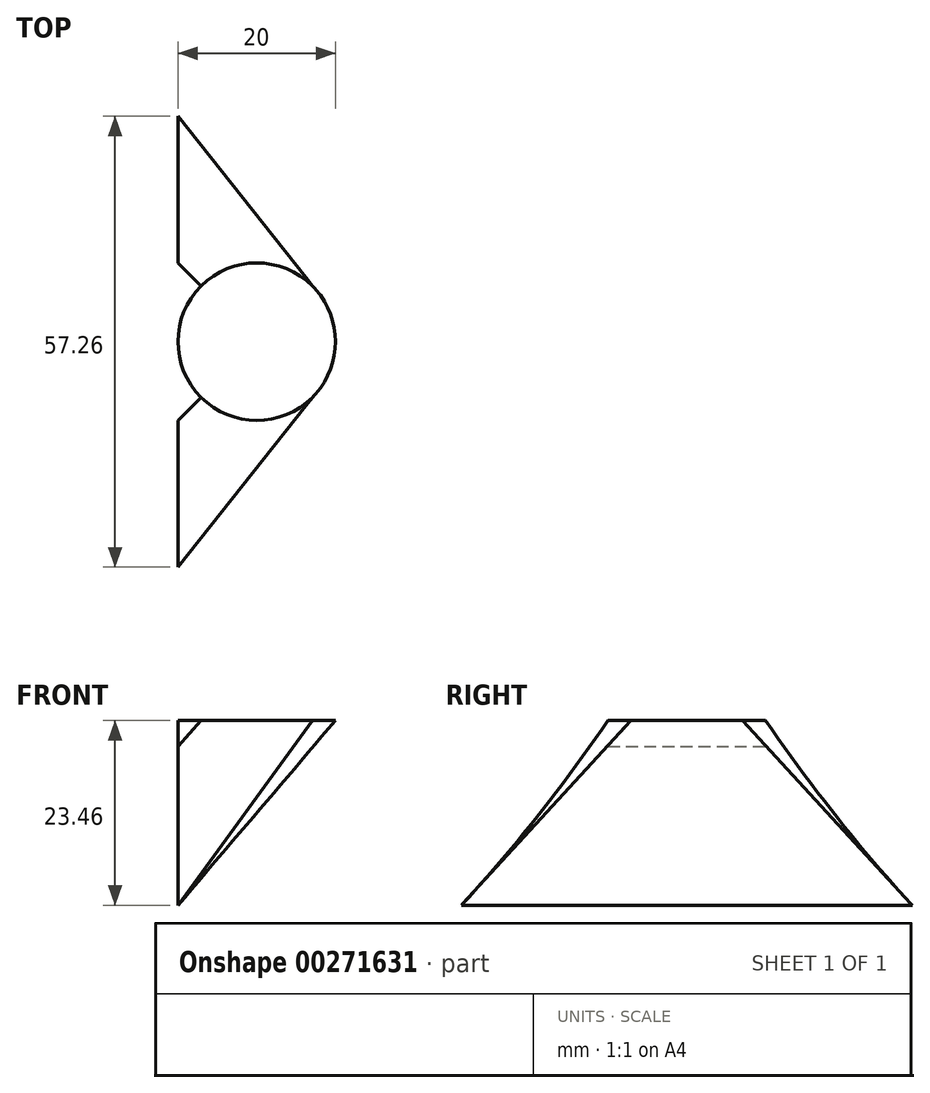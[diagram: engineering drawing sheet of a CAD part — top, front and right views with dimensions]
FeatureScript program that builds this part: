
annotation { "Feature Type Name" : "Feature", "Feature Type Description" : "" }
export const myFeature = defineFeature(function(context is Context, id is Id, definition is map)
    precondition{}
    {
        {
            var Q0;
            Q0=qCreatedBy(makeId("Top.planeOp"),FACE);
            var sketch = newSketch(context, id + "F0", { "sketchPlane" : qUnion([Q0])});
            skCircle(sketch, "E0", {"center": v(0, 0) * mm, "radius": 10 * mm});
            skLineSegment(sketch, "E1", {"start": v(0, 10) * mm, "end": v(0, -10) * mm, "construction": true});
            skLineSegment(sketch, "E2", {"start": v(10, 0) * mm, "end": v(-10, 0) * mm, "construction": true});
            skSolve(sketch);
        }
        {
            var Q0;
            Q0=sQuery(id+"F0.wireOp",VERTEX,"E2.end");
            var Q1;
            Q1=qCreatedBy(makeId("Right.planeOp"),FACE);
            cPlane(context, id + "F1", {"entities" : qUnion([Q0, Q1]), "cplaneType" : CPlaneType.PLANE_POINT, "offset" : 25 * mm, "width" : 150 * mm, "height" : 150 * mm});
        }
        {
            var Q0;
            Q0=qCreatedBy(id+"F1.planeOp",FACE);
            var sketch = newSketch(context, id + "F2", { "sketchPlane" : qUnion([Q0])});
            skLineSegment(sketch, "E3.bottom", {"start": v(-10, -3.27) * mm, "end": v(10, -3.27) * mm});
            skLineSegment(sketch, "E3.top", {"start": v(-28.63, -23.46) * mm, "end": v(28.63, -23.46) * mm});
            skLineSegment(sketch, "E3.left", {"start": v(-10, -3.27) * mm, "end": v(-28.63, -23.46) * mm});
            skLineSegment(sketch, "E3.right", {"start": v(10, -3.27) * mm, "end": v(28.63, -23.46) * mm});
            skLineSegment(sketch, "E4", {"start": v(0, -3.27) * mm, "end": v(0, -23.46) * mm, "construction": true});
            skSolve(sketch);
        }
        {
            var Q0;
            Q0=makeQuery(id+"F0.imprint","IMPRINT",FACE,{"disambiguationData":[TD([[makeQuery(id+"F0.imprint","IMPRINT",EDGE,{"derivedFrom":sQuery(id+"F0.wireOp",EDGE,"E0")}),1.0]])]});
            var Q1;
            {var subQ0=sQuery(id+"F2.wireOp",EDGE,"E3.left");Q1=makeQuery(id+"F2.imprint","IMPRINT",FACE,{"disambiguationData":[TD([[makeQuery(id+"F2.imprint","IMPRINT",EDGE,{"derivedFrom":subQ0}),1.0]])]});}
            loft(context, id + "F3", {"sheetProfilesArray" : [{ "sheetProfileEntities" : qUnion([Q0]) }, { "sheetProfileEntities" : qUnion([Q1]) }]});
        }
    });
